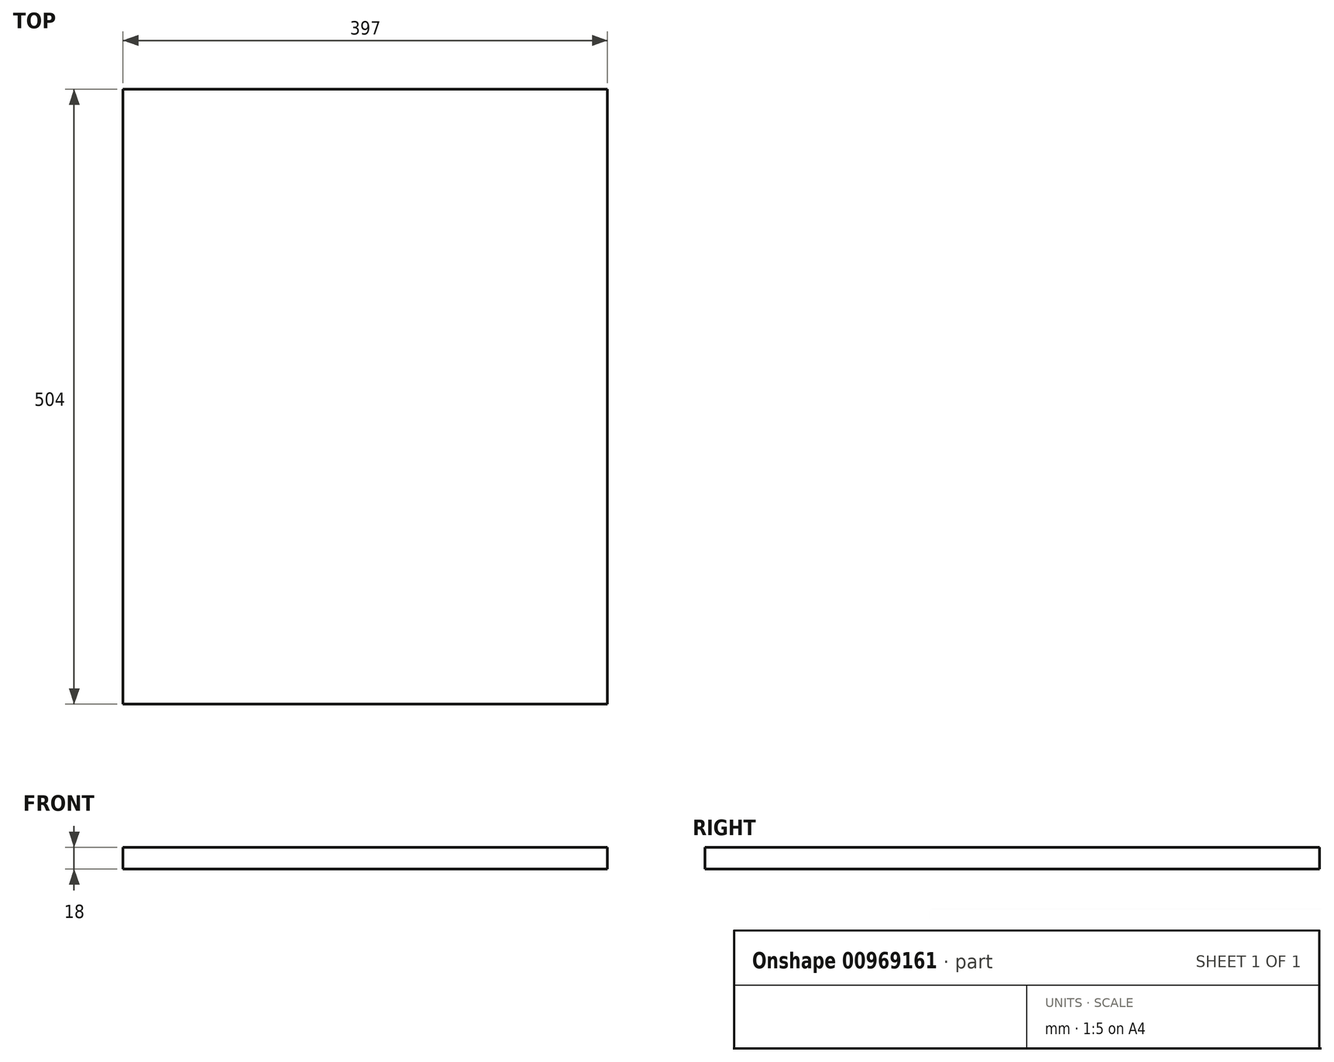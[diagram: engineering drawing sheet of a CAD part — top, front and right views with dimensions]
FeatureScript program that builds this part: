
annotation { "Feature Type Name" : "Feature", "Feature Type Description" : "" }
export const myFeature = defineFeature(function(context is Context, id is Id, definition is map)
    precondition{}
    {
        {
            var Q0;
            Q0=qCreatedBy(makeId("Top.planeOp"),FACE);
            var sketch = newSketch(context, id + "F0", { "sketchPlane" : qUnion([Q0])});
            skLineSegment(sketch, "E0.bottom", {"start": v(0, 0) * mm, "end": v(397, 0) * mm});
            skLineSegment(sketch, "E0.top", {"start": v(0, 504) * mm, "end": v(397, 504) * mm});
            skLineSegment(sketch, "E0.left", {"start": v(0, 0) * mm, "end": v(0, 504) * mm});
            skLineSegment(sketch, "E0.right", {"start": v(397, 0) * mm, "end": v(397, 504) * mm});
            skSolve(sketch);
        }
        {
            var Q0;
            Q0 = qSketchRegion(id + "F0", true);
            extrude(context, id + "F1", {"entities" : qUnion([Q0]), "depth" : 18 * mm, "offsetDistance" : 25 * mm});
        }
    });
